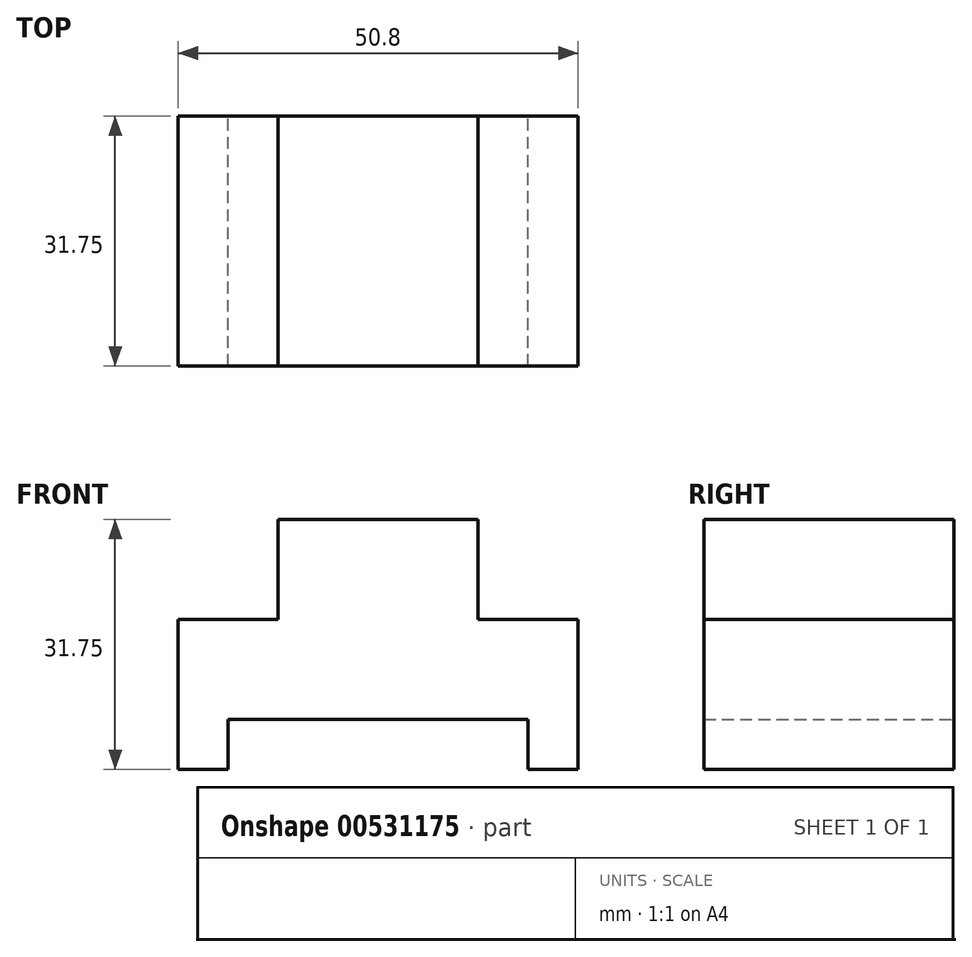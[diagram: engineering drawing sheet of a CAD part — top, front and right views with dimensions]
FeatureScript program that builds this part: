
annotation { "Feature Type Name" : "Feature", "Feature Type Description" : "" }
export const myFeature = defineFeature(function(context is Context, id is Id, definition is map)
    precondition{}
    {
        {
            var Q0;
            Q0=qCreatedBy(makeId("Top.planeOp"),FACE);
            var sketch = newSketch(context, id + "F0", { "sketchPlane" : qUnion([Q0])});
            skLineSegment(sketch, "E0", {"start": v(0, 0) * mm, "end": v(50.8, 0) * mm});
            skLineSegment(sketch, "E1", {"start": v(50.8, 0) * mm, "end": v(50.8, -31.75) * mm});
            skLineSegment(sketch, "E2", {"start": v(50.8, -31.75) * mm, "end": v(0, -31.75) * mm});
            skLineSegment(sketch, "E3", {"start": v(0, -31.75) * mm, "end": v(0, 0) * mm});
            skSolve(sketch);
        }
        {
            var Q0;
            Q0=makeQuery(id+"F0.imprint","IMPRINT",FACE,{"disambiguationData":[TD([[makeQuery(id+"F0.imprint","IMPRINT",EDGE,{"derivedFrom":sQuery(id+"F0.wireOp",EDGE,"E0")}),-1.0]])]});
            extrude(context, id + "F1", {"entities" : qUnion([Q0]), "depth" : 31.75 * mm, "offsetDistance" : 25.4 * mm});
        }
        {
            var Q0;
            Q0=qCreatedBy(makeId("Front.planeOp"),FACE);
            var sketch = newSketch(context, id + "F2", { "sketchPlane" : qUnion([Q0])});
            skLineSegment(sketch, "E4", {"start": v(0, 0) * mm, "end": v(0, 19.05) * mm});
            skLineSegment(sketch, "E5", {"start": v(0, 19.05) * mm, "end": v(12.7, 19.05) * mm});
            skLineSegment(sketch, "E6", {"start": v(12.7, 19.05) * mm, "end": v(12.7, 31.75) * mm});
            skLineSegment(sketch, "E7", {"start": v(12.7, 31.75) * mm, "end": v(38.1, 31.75) * mm});
            skLineSegment(sketch, "E8", {"start": v(38.1, 31.75) * mm, "end": v(38.1, 19.05) * mm});
            skLineSegment(sketch, "E9", {"start": v(38.1, 19.05) * mm, "end": v(50.8, 19.05) * mm});
            skLineSegment(sketch, "E10", {"start": v(50.8, 19.05) * mm, "end": v(50.8, 31.75) * mm});
            skLineSegment(sketch, "E11", {"start": v(50.8, 31.75) * mm, "end": v(38.1, 31.75) * mm});
            skLineSegment(sketch, "E12", {"start": v(0, 0) * mm, "end": v(6.35, 0) * mm});
            skPoint(sketch, "E12.endSnap0", {"position": v(6.35, 19.05) * mm});
            skLineSegment(sketch, "E13", {"start": v(6.35, 0) * mm, "end": v(6.35, 6.35) * mm});
            skLineSegment(sketch, "E14", {"start": v(6.35, 6.35) * mm, "end": v(44.45, 6.35) * mm});
            skLineSegment(sketch, "E15", {"start": v(44.45, 6.35) * mm, "end": v(44.45, 0) * mm});
            skLineSegment(sketch, "E16", {"start": v(44.45, 0) * mm, "end": v(50.8, 0) * mm});
            skLineSegment(sketch, "E17", {"start": v(50.8, 0) * mm, "end": v(50.8, 6.35) * mm});
            skLineSegment(sketch, "E18", {"start": v(50.8, 6.35) * mm, "end": v(44.45, 6.35) * mm});
            skLineSegment(sketch, "E19", {"start": v(6.35, 6.35) * mm, "end": v(0, 6.35) * mm});
            skLineSegment(sketch, "E20", {"start": v(12.7, 31.75) * mm, "end": v(0, 31.75) * mm});
            skLineSegment(sketch, "E21", {"start": v(0, 31.75) * mm, "end": v(0, 19.05) * mm});
            skLineSegment(sketch, "E22", {"start": v(44.45, 0) * mm, "end": v(6.35, 0) * mm});
            skSolve(sketch);
        }
        {
            var Q0;
            Q0=makeQuery(id+"F2.imprint","IMPRINT",FACE,{"disambiguationData":[TD([[makeQuery(id+"F2.imprint","IMPRINT",EDGE,{"derivedFrom":sQuery(id+"F2.wireOp",EDGE,"E5")}),1.0]])]});
            var Q1;
            Q1=makeQuery(id+"F2.imprint","IMPRINT",FACE,{"disambiguationData":[TD([[makeQuery(id+"F2.imprint","IMPRINT",EDGE,{"derivedFrom":sQuery(id+"F2.wireOp",EDGE,"E8")}),1.0]])]});
            var Q2;
            Q2=makeQuery(id+"F2.imprint","IMPRINT",FACE,{"disambiguationData":[TD([[makeQuery(id+"F2.imprint","IMPRINT",EDGE,{"derivedFrom":sQuery(id+"F2.wireOp",EDGE,"E13")}),-1.0]])]});
            extrude(context, id + "F3", {"entities" : qUnion([Q0, Q1, Q2]), "operationType" : NewBodyOperationType.REMOVE, "depth" : 56.64 * mm, "offsetDistance" : 25.4 * mm});
        }
    });
